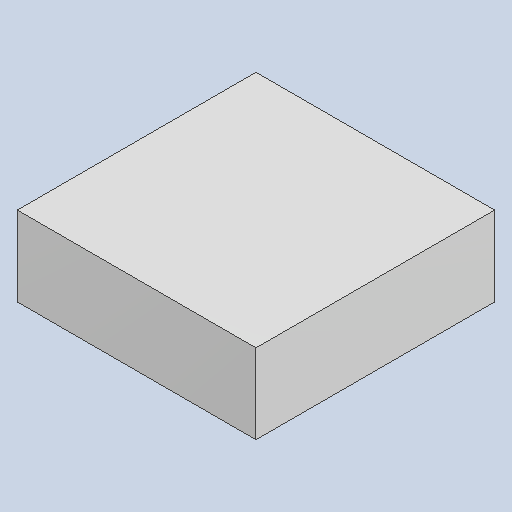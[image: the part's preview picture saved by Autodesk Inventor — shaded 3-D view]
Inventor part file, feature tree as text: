
AUTODESK INVENTOR PART (.ipt)
format: ipt  version: 2023.4 (Build 274418000, 418)  size: 79,872 bytes
history: native  units: mm
features: extrude x1
ambient origin geometry x8: Origin, YZ Plane, XZ Plane, XY Plane, X Axis, Y Axis, Z Axis, Center Point
bodies: Solid1 (feature_tree)
feature tree (1):
  extrude  "Extruded_27"  [1 undecoded]
note: 1 required parameter value undecoded (feature->parameter linkage not recoverable at this tier; creation-order binding heuristic only, values carry confidence <= 0.55)
